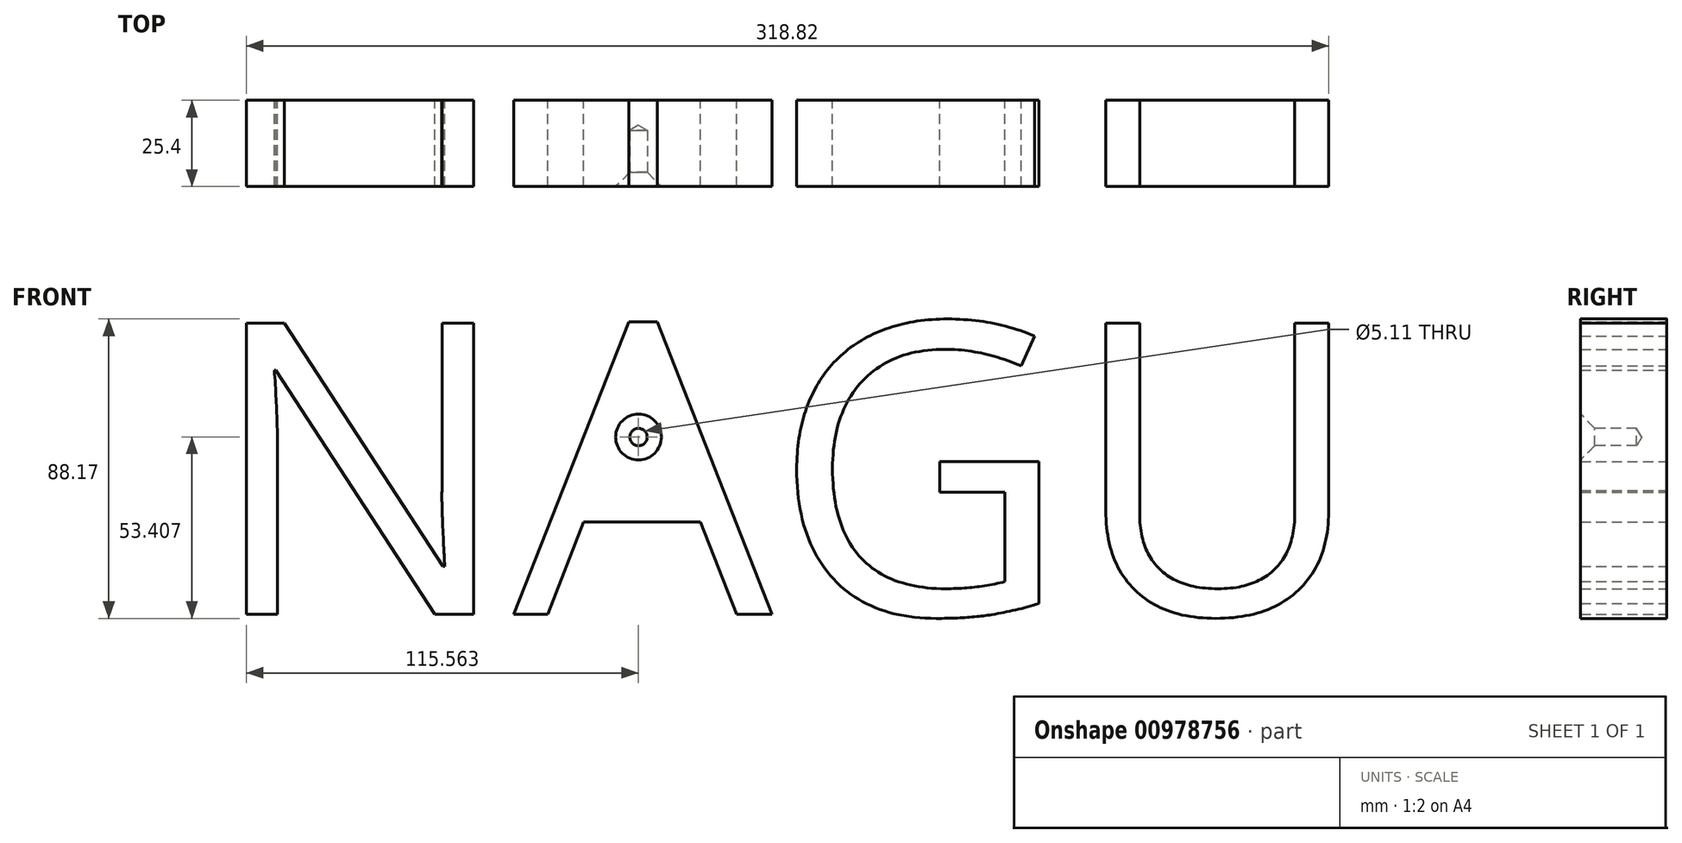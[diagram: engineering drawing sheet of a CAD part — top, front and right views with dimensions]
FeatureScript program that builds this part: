
annotation { "Feature Type Name" : "Feature", "Feature Type Description" : "" }
export const myFeature = defineFeature(function(context is Context, id is Id, definition is map)
    precondition{}
    {
        {
            var Q0;
            Q0=qCreatedBy(makeId("Front.planeOp"),FACE);
            var sketch = newSketch(context, id + "F0", { "sketchPlane" : qUnion([Q0])});
            skText(sketch, "E0", { "text": "NAGU", "fontName": "OpenSans-Regular.ttf"});
            const initialGuessF0  = {"E0": [-0.076, 0, 1, 0, 0.0865]};
            skSetInitialGuess(sketch, initialGuessF0);
            skSolve(sketch);
        }
        {
            var Q0;
            Q0=makeQuery(id+"F0.imprint","IMPRINT",FACE,{"disambiguationData":[TD([[makeQuery(id+"F0.imprint","IMPRINT",EDGE,{"derivedFrom":sQuery(id+"F0.wireOp",EDGE,"E0.sketch_text.stroke-0")}),-1.0]])]});
            var Q1;
            Q1=makeQuery(id+"F0.imprint","IMPRINT",FACE,{"disambiguationData":[TD([[makeQuery(id+"F0.imprint","IMPRINT",EDGE,{"derivedFrom":sQuery(id+"F0.wireOp",EDGE,"E0.sketch_text.stroke-28")}),-1.0]])]});
            var Q2;
            Q2=makeQuery(id+"F0.imprint","IMPRINT",FACE,{"disambiguationData":[TD([[makeQuery(id+"F0.imprint","IMPRINT",EDGE,{"derivedFrom":sQuery(id+"F0.wireOp",EDGE,"E0.sketch_text.stroke-23")}),1.0]])]});
            var Q3;
            Q3=makeQuery(id+"F0.imprint","IMPRINT",FACE,{"disambiguationData":[TD([[makeQuery(id+"F0.imprint","IMPRINT",EDGE,{"derivedFrom":sQuery(id+"F0.wireOp",EDGE,"E0.sketch_text.stroke-15")}),-1.0]])]});
            var Q4;
            Q4=makeQuery(id+"F0.imprint","IMPRINT",FACE,{"disambiguationData":[TD([[makeQuery(id+"F0.imprint","IMPRINT",EDGE,{"derivedFrom":sQuery(id+"F0.wireOp",EDGE,"E0.sketch_text.stroke-48")}),-1.0]])]});
            extrude(context, id + "F1", {"entities" : qUnion([Q0, Q1, Q2, Q3, Q4]), "depth" : 25.4 * mm, "offsetDistance" : 25.4 * mm});
        }
        {
            assignVariable(context, id + "F2", {"name" : "n", "anyValue" : 90});
        }
        {
            var Q0;
            Q0=makeQuery(id+"F1.opExtrude","CAP_FACE",FACE,{"disambiguationData":[OSD([sQuery(id+"F0.wireOp",EDGE,"E0.sketch_text.stroke-15"),sQuery(id+"F0.wireOp",EDGE,"E0.sketch_text.stroke-16"),sQuery(id+"F0.wireOp",EDGE,"E0.sketch_text.stroke-17"),sQuery(id+"F0.wireOp",EDGE,"E0.sketch_text.stroke-18"),sQuery(id+"F0.wireOp",EDGE,"E0.sketch_text.stroke-19"),sQuery(id+"F0.wireOp",EDGE,"E0.sketch_text.stroke-20"),sQuery(id+"F0.wireOp",EDGE,"E0.sketch_text.stroke-21"),sQuery(id+"F0.wireOp",EDGE,"E0.sketch_text.stroke-22")])],"isStart":false});
            var sketch = newSketch(context, id + "F3", { "sketchPlane" : qUnion([Q0])});
            skPoint(sketch, "E1", {"position": v(51.35, 52.23) * mm});
            skSolve(sketch);
        }
        {
            var Q0;
            Q0=sQuery(id+"F3.wireOp",VERTEX,"E1");
            var Q1;
            Q1=makeQuery(id+"F1.opExtrude","SWEPT_BODY",BODY,{"disambiguationData":[OSD([sQuery(id+"F0.wireOp",EDGE,"E0.sketch_text.stroke-15"),sQuery(id+"F0.wireOp",EDGE,"E0.sketch_text.stroke-16"),sQuery(id+"F0.wireOp",EDGE,"E0.sketch_text.stroke-17"),sQuery(id+"F0.wireOp",EDGE,"E0.sketch_text.stroke-18"),sQuery(id+"F0.wireOp",EDGE,"E0.sketch_text.stroke-19"),sQuery(id+"F0.wireOp",EDGE,"E0.sketch_text.stroke-20"),sQuery(id+"F0.wireOp",EDGE,"E0.sketch_text.stroke-21"),sQuery(id+"F0.wireOp",EDGE,"E0.sketch_text.stroke-22")])]});
            hole(context, id + "F4", {"style" : HoleStyle.C_SINK, "endStyle" : HoleEndStyle.BLIND, "standardTappedOrClearance" : lookupTablePath({ "standard" : "ANSI", "engagement" : "75%", "pitch" : "20 tpi", "size" : "1/4", "type" : "Tapped" }), "standardBlindInLast" : lookupTablePath({ "standard" : "ANSI", "fit" : "Normal", "engagement" : "75%", "pitch" : "20 tpi", "size" : "1/4", "type" : "Clearance & tapped" }), "holeDiameter" : 5.1 * mm, "cSinkDiameter" : 13.5 * mm, "cSinkAngle" : (getVariable(context, 'n')) * degree, "majorDiameter" : 6.35 * mm, "showTappedDepth" : true, "holeDepth" : 16.51 * mm, "isTappedThrough" : true, "tappedDepth" : 12.7 * mm, "tapClearance" : 3, "startFromSketch" : true, "locations" : qUnion([Q0]), "scope" : qUnion([Q1])});
        }
    });
